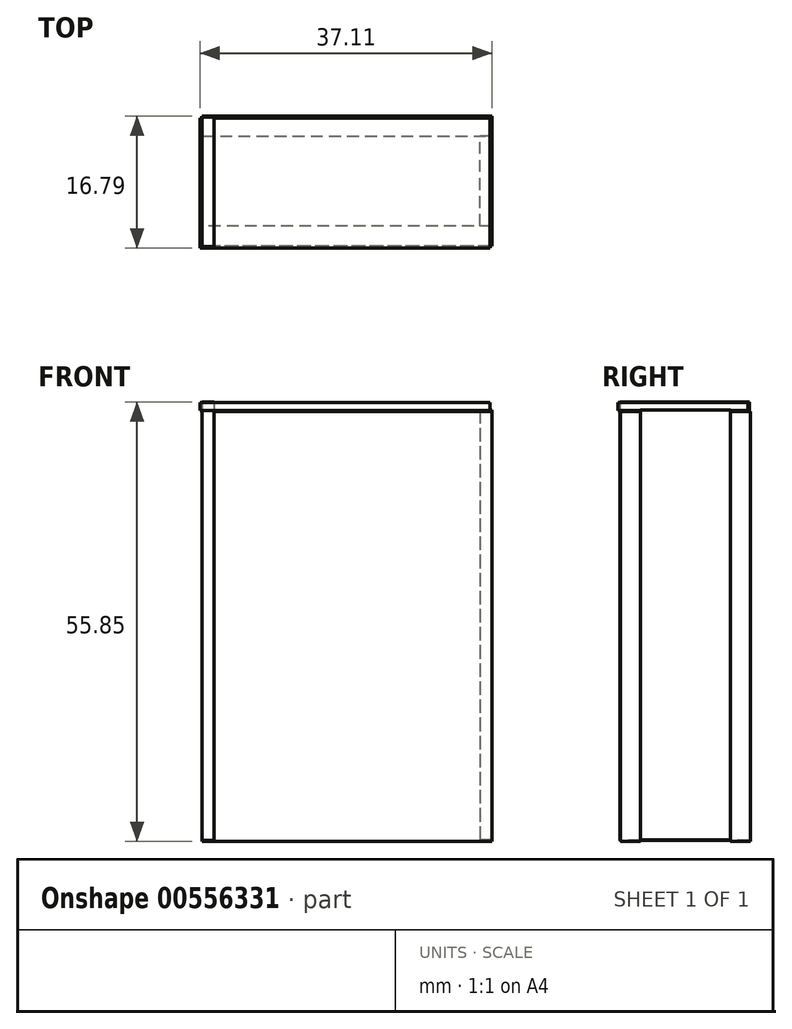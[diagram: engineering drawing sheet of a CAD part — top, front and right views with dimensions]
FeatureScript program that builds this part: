
annotation { "Feature Type Name" : "Feature", "Feature Type Description" : "" }
export const myFeature = defineFeature(function(context is Context, id is Id, definition is map)
    precondition{}
    {
        {
            var Q0;
            Q0=qCreatedBy(makeId("Front.planeOp"),FACE);
            var sketch = newSketch(context, id + "F0", { "sketchPlane" : qUnion([Q0])});
            skLineSegment(sketch, "E0.bottom", {"start": v(18.42, -27.3) * mm, "end": v(-18.41, -27.3) * mm});
            skLineSegment(sketch, "E0.top", {"start": v(18.42, 27.3) * mm, "end": v(-18.41, 27.3) * mm});
            skLineSegment(sketch, "E0.left", {"start": v(18.42, -27.3) * mm, "end": v(18.42, 27.3) * mm});
            skLineSegment(sketch, "E0.right", {"start": v(-18.41, -27.3) * mm, "end": v(-18.41, 27.3) * mm});
            skPoint(sketch, "E0.middle", {"position": v(0, 0) * mm});
            skSolve(sketch);
        }
        {
            var Q0;
            Q0=qCreatedBy(makeId("Right.planeOp"),FACE);
            var sketch = newSketch(context, id + "F1", { "sketchPlane" : qUnion([Q0])});
            skLineSegment(sketch, "E1.bottom", {"start": v(0, 27.53) * mm, "end": v(11.43, 27.53) * mm});
            skLineSegment(sketch, "E1.top", {"start": v(0, -27.08) * mm, "end": v(11.43, -27.08) * mm});
            skLineSegment(sketch, "E1.left", {"start": v(0, 27.53) * mm, "end": v(0, -27.08) * mm});
            skLineSegment(sketch, "E1.right", {"start": v(11.43, 27.53) * mm, "end": v(11.43, -27.08) * mm});
            skSolve(sketch);
        }
        {
            var Q0;
            Q0=qCreatedBy(makeId("Front.planeOp"),FACE);
            var sketch = newSketch(context, id + "F2", { "sketchPlane" : qUnion([Q0])});
            skLineSegment(sketch, "E2.bottom", {"start": v(-18.41, -27.3) * mm, "end": v(18.42, -27.3) * mm});
            skLineSegment(sketch, "E2.top", {"start": v(-18.42, 27.3) * mm, "end": v(18.41, 27.3) * mm});
            skLineSegment(sketch, "E2.left", {"start": v(-18.41, -27.3) * mm, "end": v(-18.42, 27.3) * mm});
            skLineSegment(sketch, "E2.right", {"start": v(18.42, -27.3) * mm, "end": v(18.41, 27.3) * mm});
            skPoint(sketch, "E2.middle", {"position": v(0, 0) * mm});
            skSolve(sketch);
        }
        {
            var Q0;
            Q0 = qSketchRegion(id + "F0", true);
            extrude(context, id + "F3", {"entities" : qUnion([Q0]), "depth" : 2.54 * mm, "offsetDistance" : 25.4 * mm});
        }
        {
            var Q0;
            Q0 = qSketchRegion(id + "F2", true);
            extrude(context, id + "F4", {"entities" : qUnion([Q0]), "oppositeDirection" : true, "depth" : 13.97 * mm, "offsetDistance" : 25.4 * mm, "hasSecondDirection" : true, "secondDirectionOppositeDirection" : true, "secondDirectionDepth" : 11.43 * mm});
        }
        {
            var Q0;
            Q0 = qSketchRegion(id + "F1", true);
            extrude(context, id + "F5", {"entities" : qUnion([Q0]), "depth" : 18.41 * mm, "offsetDistance" : 25.4 * mm, "hasSecondDirection" : true, "secondDirectionOppositeDirection" : false, "secondDirectionDepth" : 16.9 * mm});
        }
        {
            var Q0;
            Q0=qCreatedBy(makeId("Top.planeOp"),FACE);
            var sketch = newSketch(context, id + "F6", { "sketchPlane" : qUnion([Q0])});
            skLineSegment(sketch, "E3.bottom", {"start": v(18.13, 13.69) * mm, "end": v(-18.7, 13.69) * mm});
            skLineSegment(sketch, "E3.top", {"start": v(18.13, -2.82) * mm, "end": v(-18.7, -2.82) * mm});
            skLineSegment(sketch, "E3.left", {"start": v(18.13, 13.69) * mm, "end": v(18.13, -2.82) * mm});
            skLineSegment(sketch, "E3.right", {"start": v(-18.7, 13.69) * mm, "end": v(-18.7, -2.82) * mm});
            skSolve(sketch);
        }
        {
            var Q0;
            Q0 = qSketchRegion(id + "F6", true);
            extrude(context, id + "F7", {"entities" : qUnion([Q0]), "depth" : 28.45 * mm, "offsetDistance" : 25.4 * mm, "hasSecondDirection" : true, "secondDirectionOppositeDirection" : false, "secondDirectionDepth" : 27.43 * mm});
        }
        {
            var Q0;
            Q0=qCreatedBy(makeId("Right.planeOp"),FACE);
            var sketch = newSketch(context, id + "F8", { "sketchPlane" : qUnion([Q0])});
            skLineSegment(sketch, "E4.bottom", {"start": v(13.86, 28.55) * mm, "end": v(-2.59, 28.55) * mm});
            skLineSegment(sketch, "E4.top", {"start": v(13.86, -27.2) * mm, "end": v(-2.59, -27.2) * mm});
            skLineSegment(sketch, "E4.left", {"start": v(13.86, 28.55) * mm, "end": v(13.86, -27.2) * mm});
            skLineSegment(sketch, "E4.right", {"start": v(-2.59, 28.55) * mm, "end": v(-2.59, -27.2) * mm});
            skSolve(sketch);
        }
        {
            var Q0;
            Q0=makeQuery(id+"F8.imprint","IMPRINT",FACE,{"disambiguationData":[TD([[makeQuery(id+"F8.imprint","IMPRINT",EDGE,{"derivedFrom":sQuery(id+"F8.wireOp",EDGE,"E4.bottom")}),1.0]])]});
            extrude(context, id + "F9", {"entities" : qUnion([Q0]), "oppositeDirection" : true, "depth" : 18.41 * mm, "offsetDistance" : 25.4 * mm, "hasSecondDirection" : true, "secondDirectionOppositeDirection" : true, "secondDirectionDepth" : 16.9 * mm});
        }
    });
